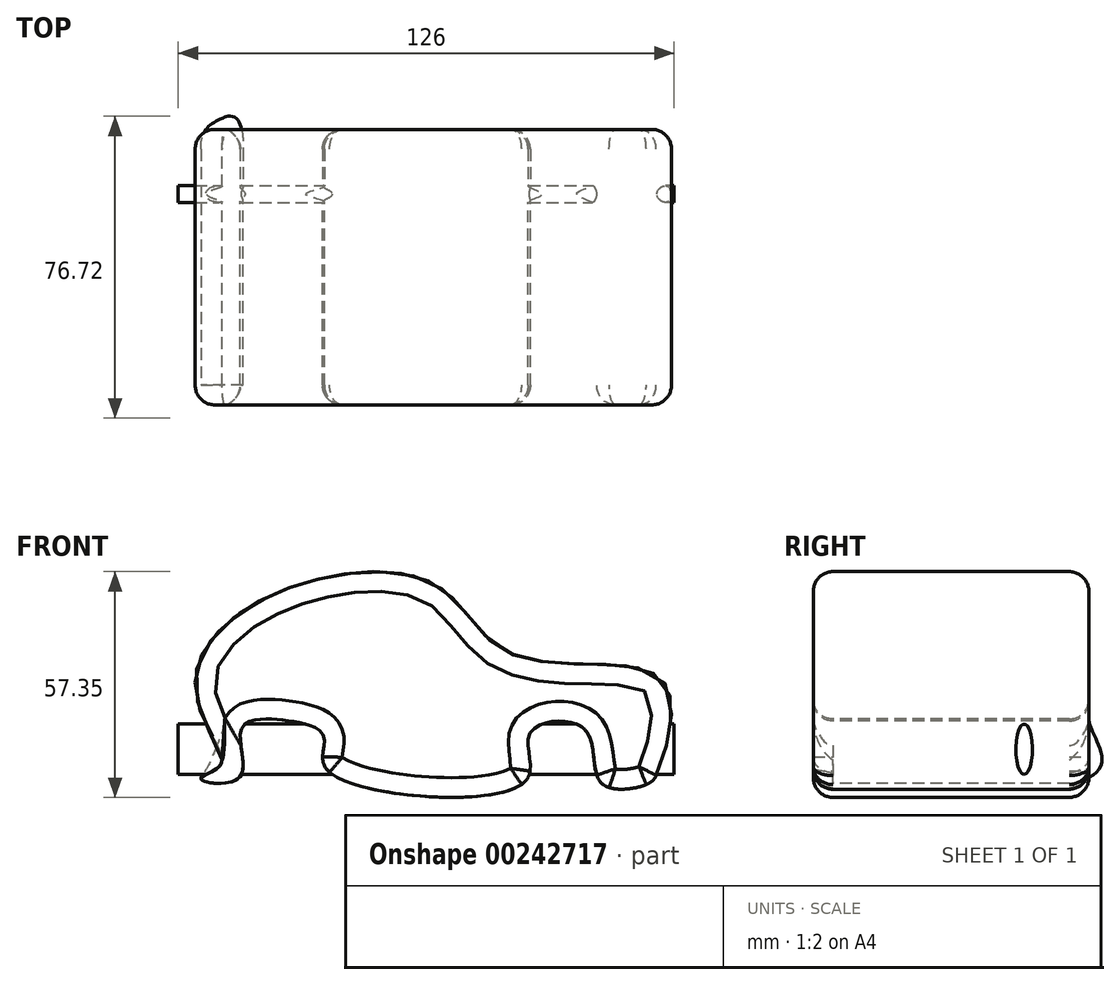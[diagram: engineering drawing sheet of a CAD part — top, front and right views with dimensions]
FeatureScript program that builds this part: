
annotation { "Feature Type Name" : "Feature", "Feature Type Description" : "" }
export const myFeature = defineFeature(function(context is Context, id is Id, definition is map)
    precondition{}
    {
        {
            var Q0;
            Q0=qCreatedBy(makeId("Front.planeOp"),FACE);
            var sketch = newSketch(context, id + "F0", { "sketchPlane" : qUnion([Q0])});
            skFitSpline(sketch, "E0", {"points": [v(-54.2, -26.32) * mm, v(-44.63, -26.11) * mm, v(-44, -13.84) * mm, v(-33.6, -11.34) * mm, v(-23, -15.5) * mm, v(-21.95, -24.24) * mm, v(27.98, -27.15) * mm, v(29.44, -14.67) * mm, v(43.17, -13.63) * mm, v(47.33, -27.15) * mm, v(58.36, -27.99) * mm, v(62.1, -24.03) * mm, v(64.6, -3.85) * mm, v(50.87, 2.6) * mm, v(22.37, 6.55) * mm, v(4.68, 23.4) * mm, v(-36.1, 20.5) * mm, v(-55.24, 1.77) * mm, v(-52.12, -14.05) * mm, v(-49.41, -23) * mm, v(-54.2, -26.32) * mm]});
            skSolve(sketch);
        }
        {
            var Q0;
            Q0 = qSketchRegion(id + "F0", true);
            var Q1;
            Q1 = qSketchRegion(id + "FYGrevhfaanhLYz_1", true);
            extrude(context, id + "F1", {"entities" : qUnion([Q0, Q1]), "endBound" : BoundingType.SYMMETRIC, "depth" : 70 * mm});
        }
        {
            var Q0;
            Q0=makeQuery(id+"F1.opExtrude","CAP_EDGE",EDGE,{"disambiguationData":[OSD([sQuery(id+"F0.wireOp",EDGE,"E0")])],"isStart":false});
            fillet(context, id + "F2", {"entities" : qUnion([Q0]), "radius" : 5 * mm, "tangentPropagation" : true, "allowEdgeOverflow" : false});
        }
        {
            var Q0;
            Q0=makeQuery(id+"F1.opExtrude","CAP_EDGE",EDGE,{"disambiguationData":[OSD([sQuery(id+"F0.wireOp",EDGE,"E0")])],"isStart":true});
            fillet(context, id + "F3", {"entities" : qUnion([Q0]), "radius" : 5 * mm, "tangentPropagation" : true, "allowEdgeOverflow" : false});
        }
        {
            var Q0;
            Q0=qCreatedBy(makeId("Right.planeOp"),FACE);
            var sketch = newSketch(context, id + "F4", { "sketchPlane" : qUnion([Q0])});
            skEllipse(sketch, "E1", {"center": v(18.57, -18.76) * mm, "majorRadius": 6.4 * mm, "minorRadius": 2.12 * mm, "majorAxis": v(0, -1)});
            skSolve(sketch);
        }
        {
            var Q0;
            Q0 = qSketchRegion(id + "F4", true);
            extrude(context, id + "F5", {"entities" : qUnion([Q0]), "operationType" : NewBodyOperationType.ADD, "depth" : 66 * mm, "hasSecondDirection" : true, "secondDirectionOppositeDirection" : true, "secondDirectionDepth" : 60 * mm});
        }
    });
